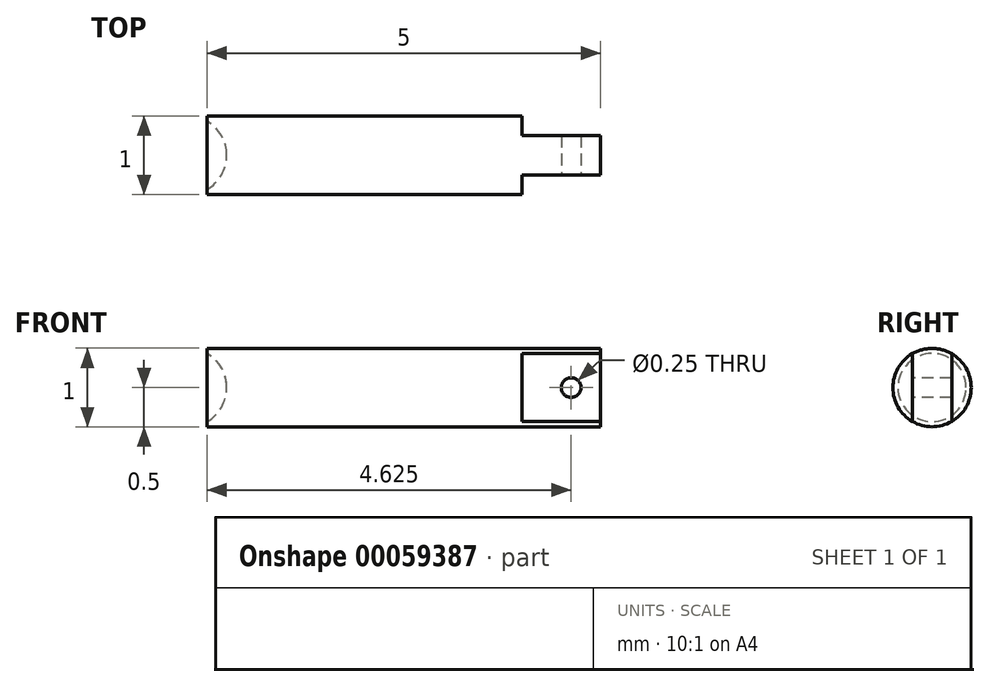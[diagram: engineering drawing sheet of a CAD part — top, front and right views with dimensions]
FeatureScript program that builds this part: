
annotation { "Feature Type Name" : "Feature", "Feature Type Description" : "" }
export const myFeature = defineFeature(function(context is Context, id is Id, definition is map)
    precondition{}
    {
        {
            var Q0;
            Q0=qCreatedBy(makeId("Front.planeOp"),FACE);
            var sketch = newSketch(context, id + "F0", { "sketchPlane" : qUnion([Q0])});
            skLineSegment(sketch, "E0.bottom", {"start": v(0, 0) * mm, "end": v(5, 0) * mm});
            skLineSegment(sketch, "E0.top", {"start": v(0, 0.5) * mm, "end": v(5, 0.5) * mm});
            skLineSegment(sketch, "E0.left", {"start": v(0, 0) * mm, "end": v(0, 0.5) * mm});
            skLineSegment(sketch, "E0.right", {"start": v(5, 0) * mm, "end": v(5, 0.5) * mm});
            skArc(sketch, "E1", {"start": v(0, 0.43) * mm, "mid": v(0.18, 0.25) * mm, "end": v(0.25, 0) * mm});
            skSolve(sketch);
        }
        {
            var Q0;
            {var subQ2=sQuery(id+"F0.wireOp",EDGE,"E0.top");Q0=makeQuery(id+"F0.imprint","IMPRINT",FACE,{"disambiguationData":[TD([[makeQuery(id+"F0.imprint","IMPRINT",EDGE,{"derivedFrom":subQ2}),-1.0]])]});}
            var Q1;
            Q1=sQuery(id+"F0.wireOp",EDGE,"E0.bottom");
            revolve(context, id + "F1", {"entities" : qUnion([Q0]), "axis" : qUnion([Q1]), "revolveType" : RevolveType.FULL});
        }
        {
            var Q0;
            Q0=makeQuery(id+"F1.opRevolve","SWEPT_FACE",FACE,{"disambiguationData":[OSD([sQuery(id+"F0.wireOp",EDGE,"E0.right")])]});
            var sketch = newSketch(context, id + "F2", { "sketchPlane" : qUnion([Q0])});
            skLineSegment(sketch, "E2.bottom", {"start": v(-1.8, 2.1) * mm, "end": v(1.95, 2.1) * mm});
            skLineSegment(sketch, "E2.top", {"start": v(-1.8, -2.53) * mm, "end": v(1.95, -2.53) * mm});
            skLineSegment(sketch, "E2.left", {"start": v(-1.8, 2.1) * mm, "end": v(-1.8, -2.53) * mm});
            skLineSegment(sketch, "E2.right", {"start": v(1.95, 2.1) * mm, "end": v(1.95, -2.53) * mm});
            skLineSegment(sketch, "E3.bottom", {"start": v(-0.25, 0.93) * mm, "end": v(0.25, 0.93) * mm});
            skLineSegment(sketch, "E3.top", {"start": v(-0.25, -1.26) * mm, "end": v(0.25, -1.26) * mm});
            skLineSegment(sketch, "E3.left", {"start": v(-0.25, 0.93) * mm, "end": v(-0.25, -1.26) * mm});
            skLineSegment(sketch, "E3.right", {"start": v(0.25, 0.93) * mm, "end": v(0.25, -1.26) * mm});
            skSolve(sketch);
        }
        {
            var Q0;
            Q0 = qSketchRegion(id + "F2", true);
            extrude(context, id + "F3", {"entities" : qUnion([Q0]), "operationType" : NewBodyOperationType.REMOVE, "oppositeDirection" : true, "depth" : 1 * mm});
        }
        {
            var Q0;
            Q0=makeQuery(id+"F3.boolean.opBoolean","COPY",FACE,{"derivedFrom":makeQuery(id+"F3.opExtrude","SWEPT_FACE",FACE,{"disambiguationData":[OSD([sQuery(id+"F2.wireOp",EDGE,"E3.left")])]})});
            var sketch = newSketch(context, id + "F4", { "sketchPlane" : qUnion([Q0])});
            skCircle(sketch, "E4", {"center": v(4.62, 0) * mm, "radius": 0.12 * mm});
            skSolve(sketch);
        }
        {
            var Q0;
            Q0 = qSketchRegion(id + "F4", true);
            extrude(context, id + "F5", {"entities" : qUnion([Q0]), "operationType" : NewBodyOperationType.REMOVE, "oppositeDirection" : true, "depth" : 1 * mm});
        }
    });
